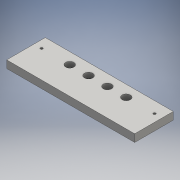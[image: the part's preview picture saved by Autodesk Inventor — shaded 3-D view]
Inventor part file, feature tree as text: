
AUTODESK INVENTOR PART (.ipt)
format: ipt  version: 2016 (Build 200138000, 138)  size: 120,320 bytes
history: native  units: mm
features: sketch x3, hole x2, extrude x1
ambient origin geometry x8: Origin, YZ Plane, XZ Plane, XY Plane, X Axis, Y Axis, Z Axis, Center Point
bodies: Solid1 (feature_tree)
feature tree (6):
  extrude  "Extrusion1"  Depth=170.0mm
  hole  "Hole1"  [1 undecoded]
  hole  "Hole2"  [1 undecoded]
  sketch  "Sketch1"  dims[d0=30.0mm d1=170.0mm]
  sketch  "Sketch2"  dims[d2=85.0mm d3=15.0mm]
  sketch  "Sketch3"  dims[d4=10.0mm d5=0.0mm d9=6.6mm d10=6.0mm d11=11.0mm d12=7.0mm d13=90.0deg d14=8.0mm d15=20.594885mm d16=150.0mm d17=75.0mm d19=3.242mm d20=8.0mm d21=19.05mm d22=4.775mm d23=90.0deg d24=11.8mm d25=20.594885mm d30=25.0mm d31=25.0mm d32=25.0mm d33=12.5mm d34=21.3mm d35=170.0mm]
note: 2 required parameter values undecoded (feature->parameter linkage not recoverable at this tier; creation-order binding heuristic only, values carry confidence <= 0.55)
